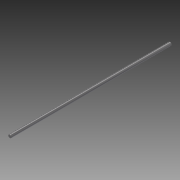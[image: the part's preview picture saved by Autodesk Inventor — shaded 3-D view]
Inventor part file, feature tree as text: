
AUTODESK INVENTOR PART (.ipt)
format: ipt  version: 2013 (Build 170138000, 138)  size: 105,472 bytes
history: native  units: in
note: dims shown in document units (in); Inventor stores cm internally (conversion verified against a paired STEP export)
features: extrude x1, other x1, imported_body x1
ambient origin geometry x8: Origin, YZ Plane, XZ Plane, XY Plane, X Axis, Y Axis, Z Axis, Center Point
feature tree (3):
  extrude  "Extrude2"  [1 undecoded]
  other  "1497K9521"
  imported_body  "Base1"
note: 1 required parameter value undecoded (feature->parameter linkage not recoverable at this tier; creation-order binding heuristic only, values carry confidence <= 0.55)
